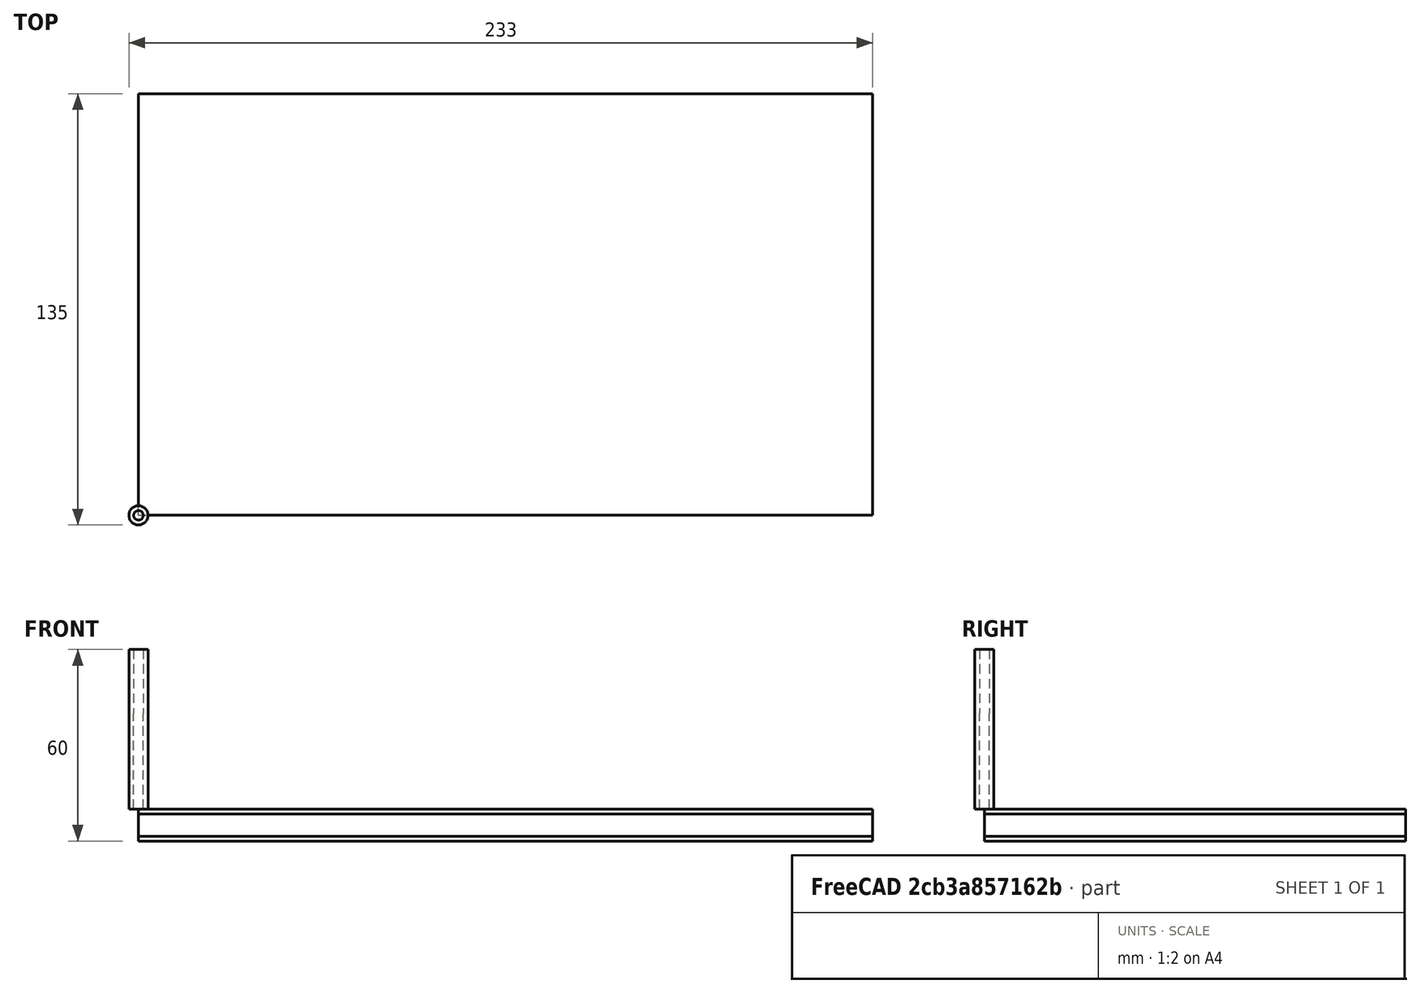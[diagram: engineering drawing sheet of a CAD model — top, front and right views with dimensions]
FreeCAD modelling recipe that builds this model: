
FCSTD DOCUMENT  (FreeCAD 0.19R24276 (Git))
Label: RD6006-AlimSupport
License: All rights reserved
LicenseURL: http://en.wikipedia.org/wiki/All_rights_reserved
objects: Path::FeaturePython×7, Part::FeaturePython×6, App::DocumentObjectGroup×4, Sketcher::SketchObject×2, App::FeaturePython×2, Path::FeatureCompoundPython×2, Mesh::FeaturePython×2, PartDesign::Pad×1, PartDesign::Pocket×1, PartDesign::Body×1
note: 15 computed .brp shape members not serialized (recipe doc carries the construction recipe); baked Part::Feature solids carry a one-line shape summary decoded from their .brp

FEATURE [Sketcher::SketchObject] Sketch
  FullyConstrained = false
  MapMode = 5
  Support = -> [XY_Plane]
  sketch-geometry (4):
    g0: LineSegment StartX=0 StartY=122 StartZ=0 EndX=220 EndY=122 EndZ=0
    g1: LineSegment StartX=220 StartY=122 StartZ=0 EndX=220 EndY=0 EndZ=0
    g2: LineSegment StartX=220 StartY=0 StartZ=0 EndX=0 EndY=0 EndZ=0
    g3: LineSegment StartX=0 StartY=0 StartZ=0 EndX=0 EndY=122 EndZ=0
  constraints (10):
    c: Coincident(g0,g1)
    c: Coincident(g1,g2)
    c: Coincident(g2,g3)
    c: Coincident(g3,g0)
    c: Horizontal(g0)
    c: Horizontal(g2)
    c: Vertical(g1)
    c: Vertical(g3)
    c: DistanceX(g0,g0) = 220
    c: DistanceY(g2,g0) = 122
FEATURE [PartDesign::Pad] Pad
  Direction = (1,1,1)
  Length = 8.5
  Length2 = 100
  Profile = -> Sketch
  Type = 0
FEATURE [Sketcher::SketchObject] Sketch001
  FullyConstrained = true
  MapMode = 5
  Placement = pos=(0,0,8.5) rot=(0,0,1;0rad)
  Support = -> [Pad]
  sketch-geometry (4):
    g0: Circle CenterX=25 CenterY=7 CenterZ=0 NormalX=0 NormalY=0 NormalZ=1 AngleXU=0 Radius=2
    g1: Circle CenterX=25 CenterY=109 CenterZ=0 NormalX=0 NormalY=0 NormalZ=1 AngleXU=0 Radius=2
    g2: Circle CenterX=197 CenterY=109 CenterZ=0 NormalX=0 NormalY=0 NormalZ=1 AngleXU=0 Radius=2
    g3: Circle CenterX=197 CenterY=7 CenterZ=0 NormalX=0 NormalY=0 NormalZ=1 AngleXU=0 Radius=2
  constraints (12):
    c: DistanceY(g-1,g0) = 7
    c: DistanceX(g-1,g0) = 25
    c: DistanceY(g-1,g1) = 109
    c: DistanceX(g-1,g1) = 25
    c: DistanceY(g-1,g3) = 7
    c: DistanceY(g-1,g2) = 109
    c: DistanceX(g0,g3) = 172
    c: DistanceX(g1,g2) = 172
    c: Radius(g1) = 2
    c: Radius(g2) = 2
    c: Radius(g3) = 2
    c: Radius(g0) = 2
FEATURE [PartDesign::Pocket] Pocket
  BaseFeature = -> Pad
  Length = 5
  Length2 = 100
  Profile = -> Sketch001
  Type = 1
FEATURE [PartDesign::Body] Body
  Group = -> [Sketch,Pad,Sketch001,Pocket]
  Origin = -> Origin
  Tip = -> Pocket
FEATURE [App::FeaturePython] SetupSheet  # Path/CAM operation (typed FeaturePython)
  ClearanceHeightExpression = OpStockZMax+SetupSheet.ClearanceHeightOffset
  ClearanceHeightOffset = 5
  CoolantMode = 0
  CoolantModes = None | Flood | Mist
  FinalDepthExpression = OpFinalDepth
  HorizRapid = 0
  SafeHeightExpression = OpStockZMax+SetupSheet.SafeHeightOffset
  SafeHeightOffset = 3
  StartDepthExpression = OpStartDepth
  StepDownExpression = OpToolDiameter
  VertRapid = 0
FEATURE [Part::FeaturePython] Clone  label="Model-Body"  # Draft clone (typed FeaturePython)
  AttacherType = Attacher::AttachEngine3D
  Fuse = false
  Objects = -> [Body]
  PathResource = Model
  Placement = pos=(5,5,-10) rot=(0,0,1;0rad)
  Scale = (1,1,1)
FEATURE [App::DocumentObjectGroup] Model
  Group = -> [Clone]
FEATURE [Part::FeaturePython] ToolBit  label="Endmill"  # Path/CAM toolbit (typed FeaturePython)
  BitPropertyNames = Chipload | CuttingEdgeHeight | Diameter | Flutes | Length | Material | ShankDiameter
  BitShape = /Volumes/SSD/Applications/FreeCAD_0.19-24276.app/Contents/Resources/Mod/Path/Tools/Shape/endmill.fcstd
  Chipload = 0
  CuttingEdgeHeight = 30
  Diameter = 6
  Flutes = 0
  Length = 50
  Material = 0
  ShankDiameter = 6
  ShapeName = endmill
FEATURE [Path::FeaturePython] TC__Default_Tool  label="TC: Default Tool"  # Path/CAM operation (typed FeaturePython)
  HorizFeed = 0
  HorizRapid = 0
  SpindleDir = 0
  SpindleSpeed = 0
  Tool = -> ToolBit
  ToolNumber = 1
  VertFeed = 0
  VertRapid = 0
  expr: HorizRapid = SetupSheet.HorizRapid
  expr: VertRapid = SetupSheet.VertRapid
FEATURE [App::DocumentObjectGroup] Tools
  Group = -> [TC__Default_Tool]
FEATURE [Part::FeaturePython] Stock  # WARN: FeaturePython — macro-defined, semantics opaque (R4)
  Base = -> Model
  ExtXneg = 5
  ExtXpos = 5
  ExtYneg = 5
  ExtYpos = 5
  ExtZneg = 0
  ExtZpos = 0
  Placement = pos=(5,5,-10) rot=(0,0,1;0rad)
  StockType = FromBase
FEATURE [Path::FeaturePython] Profile  # Path/CAM operation (typed FeaturePython)
  Active = true
  AreaParams:
    Tolerance = 1e-07
    FitArcs = True
    Simplify = False
    CleanDistance = 0.0
    Accuracy = 0.01
    Unit = 1.0
    MinArcPoints = 4
    MaxArcPoints = 100
    ClipperScale = 10000000.0
    Fill = 0
    Coplanar = 0
    Reorient = True
    Outline = False
    Explode = False
    OpenMode = 0
    Deflection = 0.01
    SubjectFill = 0
    ClipFill = 0
    Offset = 3.0
    ExtraPass = 0
    Stepover = 0.0
    LastStepover = 0.0
    JoinType = 0
    EndType = 0
    MiterLimit = 2.0
    RoundPrecision = 0.0
    PocketMode = 0
    ToolRadius = 1.0
    PocketExtraOffset = 0.0
    PocketStepover = 0.0
    PocketLastStepover = 0.0
    FromCenter = False
    Angle = 45.0
    AngleShift = 0.0
    Shift = 0.0
    Thicken = False
    SectionCount = -1
    Stepdown = 1.0
    SectionOffset = 0.0
    SectionTolerance = 1e-06
    SectionMode = 2
    Project = False
  AttemptInverseAngle = true
  Base = -> [Clone]
  ClearanceHeight = 5
  CoolantMode = None
  CycleTime = Cycletime Error
  Direction = 1
  EnableRotation = 0
  FinalDepth = -8.5
  HandleMultipleFeatures = 0
  InverseAngle = false
  JoinType = 0
  LimitDepthToFace = true
  MiterLimit = 0.1
  OffsetExtra = 0
  OpFinalDepth = -10
  OpStartDepth = -1.5
  OpStockZMax = -1.5
  OpStockZMin = -10
  OpToolDiameter = 6
  PathParams = {'orientation': 0, 'feedrate': 0.0, 'feedrate_v': 0.0, 'verbose': True, 'resume_height': 5.0, 'retraction': 5.0, 'return_end': True, 'preamble': False, 'start': Vector (0.0, 0.0, 0.0)}
  ReverseDirection = false
  SafeHeight = 5
  Side = 0
  StartDepth = 0
  StartPoint = (0,0,0)
  StepDown = 3
  ToolController = -> TC__Default_Tool
  UseComp = true
  UseStartPoint = true
  processCircles = false
  processHoles = false
  processPerimeter = true
  expr: ClearanceHeight = 5
  expr: SafeHeight = 5
  expr: StepDown = 3
  expr: FinalDepth = -8.5
  expr: StartDepth = 0
FEATURE [Path::FeaturePython] DressupTag  # Path/CAM operation (typed FeaturePython)
  Angle = 45
  Base = -> Profile
  Height = 4.25
  Positions = (4) [(60,2,0),(170,2,0),(170,130,0),(60,130,0)]
  Radius = 0
  SegmentationFactor = 50
  Width = 22
FEATURE [Path::FeatureCompoundPython] Operations  # Path/CAM operation (typed FeaturePython)
  Group = -> [DressupTag]
  UsePlacements = false
FEATURE [Path::FeaturePython] Job  label="support"  # Path/CAM operation (typed FeaturePython)
  CycleTime = 00:00:00
  Fixtures = G54
  GeometryTolerance = 0.01
  LastPostProcessDate = 2021-04-07 00:28:13.518904
  LastPostProcessOutput = /Volumes/SSD/Dev/CNC/MiscCNC/RD6006-AlimSupport.gcode
  Model = -> Model
  Operations = -> Operations
  OrderOutputBy = 0
  PostProcessor = 1
  PostProcessorOutputFile = /Volumes/SSD/Dev/CNC/MiscCNC/RD6006-AlimSupport.gcode
  SetupSheet = -> SetupSheet
  SplitOutput = false
  Stock = -> Stock
  Tools = -> Tools
FEATURE [App::FeaturePython] SetupSheet001  # Path/CAM operation (typed FeaturePython)
  ClearanceHeightExpression = OpStockZMax+SetupSheet001.ClearanceHeightOffset
  ClearanceHeightOffset = 5
  CoolantMode = 0
  CoolantModes = None | Flood | Mist
  FinalDepthExpression = OpFinalDepth
  HorizRapid = 0
  SafeHeightExpression = OpStockZMax+SetupSheet001.SafeHeightOffset
  SafeHeightOffset = 3
  StartDepthExpression = OpStartDepth
  StepDownExpression = OpToolDiameter
  VertRapid = 0
FEATURE [Part::FeaturePython] Clone001  label="Model-Body001"  # Draft clone (typed FeaturePython)
  AttacherType = Attacher::AttachEngine3D
  Fuse = false
  Objects = -> [Body]
  PathResource = Model
  Placement = pos=(5,5,-8.5) rot=(0,0,1;0rad)
  Scale = (1,1,1)
FEATURE [App::DocumentObjectGroup] Model001
  Group = -> [Clone001]
FEATURE [Part::FeaturePython] ToolBit001  label="Endmill001"  # Path/CAM toolbit (typed FeaturePython)
  BitPropertyNames = Chipload | CuttingEdgeHeight | Diameter | Flutes | Length | Material | ShankDiameter
  BitShape = /Volumes/SSD/Applications/FreeCAD_0.19-24276.app/Contents/Resources/Mod/Path/Tools/Shape/endmill.fcstd
  Chipload = 0
  CuttingEdgeHeight = 30
  Diameter = 3
  Flutes = 0
  Length = 50
  Material = 0
  ShankDiameter = 3
  ShapeName = endmill
FEATURE [Path::FeaturePython] TC__Default_Tool001  label="TC: Default Tool001"  # Path/CAM operation (typed FeaturePython)
  HorizFeed = 0
  HorizRapid = 0
  SpindleDir = 0
  SpindleSpeed = 0
  Tool = -> ToolBit001
  ToolNumber = 1
  VertFeed = 0
  VertRapid = 0
  expr: HorizRapid = SetupSheet001.HorizRapid
  expr: VertRapid = SetupSheet001.VertRapid
FEATURE [App::DocumentObjectGroup] Tools001
  Group = -> [TC__Default_Tool001]
FEATURE [Part::FeaturePython] Stock001  # WARN: FeaturePython — macro-defined, semantics opaque (R4)
  Base = -> Model001
  ExtXneg = 5
  ExtXpos = 5
  ExtYneg = 5
  ExtYpos = 5
  ExtZneg = 0
  ExtZpos = 0
  Placement = pos=(5,5,-8.5) rot=(0,0,1;0rad)
  StockType = FromBase
FEATURE [Path::FeaturePython] Profile001  # Path/CAM operation (typed FeaturePython)
  Active = true
  AreaParams:
    Tolerance = 1e-07
    FitArcs = True
    Simplify = False
    CleanDistance = 0.0
    Accuracy = 0.01
    Unit = 1.0
    MinArcPoints = 4
    MaxArcPoints = 100
    ClipperScale = 10000000.0
    Fill = 0
    Coplanar = 0
    Reorient = True
    Outline = False
    Explode = False
    OpenMode = 0
    Deflection = 0.01
    SubjectFill = 0
    ClipFill = 0
    Offset = -1.5
    ExtraPass = 0
    Stepover = 0.0
    LastStepover = 0.0
    JoinType = 0
    EndType = 0
    MiterLimit = 2.0
    RoundPrecision = 0.0
    PocketMode = 0
    ToolRadius = 1.0
    PocketExtraOffset = 0.0
    PocketStepover = 0.0
    PocketLastStepover = 0.0
    FromCenter = False
    Angle = 45.0
    AngleShift = 0.0
    Shift = 0.0
    Thicken = False
    SectionCount = -1
    Stepdown = 1.0
    SectionOffset = 0.0
    SectionTolerance = 1e-06
    SectionMode = 2
    Project = False
  AttemptInverseAngle = true
  Base = -> [Clone001]
  ClearanceHeight = 5
  CoolantMode = None
  CycleTime = Cycletime Error
  Direction = 1
  EnableRotation = 0
  FinalDepth = -8.5
  HandleMultipleFeatures = 0
  InverseAngle = false
  JoinType = 0
  LimitDepthToFace = true
  MiterLimit = 0.1
  OffsetExtra = 0
  OpFinalDepth = -8.5
  OpStartDepth = 0
  OpStockZMax = 0
  OpStockZMin = -8.5
  OpToolDiameter = 3
  PathParams = {'orientation': 0, 'feedrate': 0.0, 'feedrate_v': 0.0, 'verbose': True, 'resume_height': 5.0, 'retraction': 5.0, 'return_end': True, 'preamble': False, 'start': Vector (201.5072599590478, 113.99858836364797, 5.0)}
  ReverseDirection = false
  SafeHeight = 5
  Side = 1
  StartDepth = 0
  StartPoint = (0,0,0)
  StepDown = 3
  ToolController = -> TC__Default_Tool001
  UseComp = true
  UseStartPoint = false
  processCircles = false
  processHoles = false
  processPerimeter = true
  expr: ClearanceHeight = OpStockZMax + SetupSheet001.ClearanceHeightOffset
  expr: SafeHeight = 5
  expr: StepDown = OpToolDiameter
  expr: FinalDepth = OpFinalDepth
  expr: StartDepth = OpStartDepth
FEATURE [Path::FeatureCompoundPython] Operations001  # Path/CAM operation (typed FeaturePython)
  Group = -> [Profile001]
  UsePlacements = false
FEATURE [Path::FeaturePython] Job001  label="fixations"  # Path/CAM operation (typed FeaturePython)
  CycleTime = 00:00:00
  Fixtures = G54
  GeometryTolerance = 0.01
  LastPostProcessDate = 2021-04-07 00:28:49.031602
  LastPostProcessOutput = /Volumes/SSD/Dev/CNC/MiscCNC/RD6006-AlimFixations.gcode
  Model = -> Model001
  Operations = -> Operations001
  OrderOutputBy = 0
  PostProcessor = 1
  PostProcessorOutputFile = /Volumes/SSD/Dev/CNC/MiscCNC/RD6006-AlimFixations.gcode
  SetupSheet = -> SetupSheet001
  SplitOutput = false
  Stock = -> Stock001
  Tools = -> Tools001
FEATURE [Mesh::FeaturePython] CutMaterial  label="usinageSupport"  # WARN: FeaturePython — macro-defined, semantics opaque (R4)
FEATURE [Mesh::FeaturePython] CutMaterial001  label="usinageFixations"  # WARN: FeaturePython — macro-defined, semantics opaque (R4)
